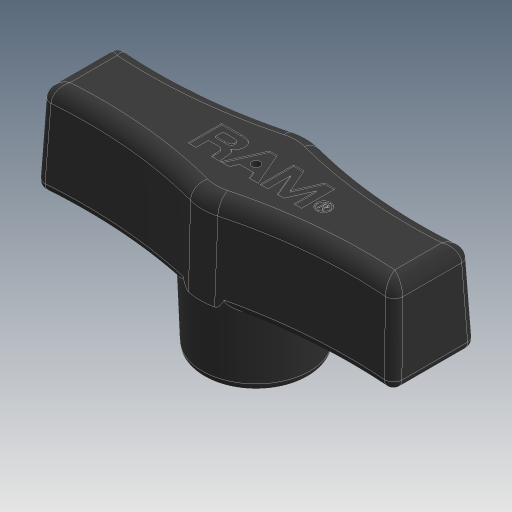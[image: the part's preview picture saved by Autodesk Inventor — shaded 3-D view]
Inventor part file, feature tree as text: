
AUTODESK INVENTOR PART (.ipt)
format: ipt  version: 2023.1 (Build 271208000, 208)  size: 791,552 bytes
history: native  units: mm
features: sketch x10, fillet x4, other x3, loft x3, revolve x2, mirror x1, thread x1, extrude x1
ambient origin geometry x8: Origin, YZ Plane, XZ Plane, XY Plane, X Axis, Y Axis, Z Axis, Center Point
bodies: Solido3 (feature_tree)
feature tree (25):
  sketch  "Schizzo4"
  other  "Piano di lavoro1"
  sketch  "Schizzo6"
  other  "Piano di lavoro2"
  sketch  "Schizzo7"
  loft  "Loft2"
  loft  "Loft3"
  other  "Piano di lavoro3"
  loft  "Loft5"
  mirror  "Specchio1"
  fillet  "Raccordo1"  Radius=14.9mm
  fillet  "Raccordo2"  Radius=14.4mm
  fillet  "Raccordo3"  Radius=19.0mm
  fillet  "Raccordo4"  Radius=62.8mm
  revolve  "Rivoluzione1"
  revolve  "Rivoluzione2"
  thread  "Filettatura1"
  extrude  "Estrusione3"  Depth=1.5mm
  sketch  "Schizzo8"
  sketch  "Schizzo9"
  sketch  "Schizzo10"
  sketch  "Schizzo12"
  sketch  "Schizzo14"
  sketch  "Schizzo16"
  sketch  "Schizzo17"
